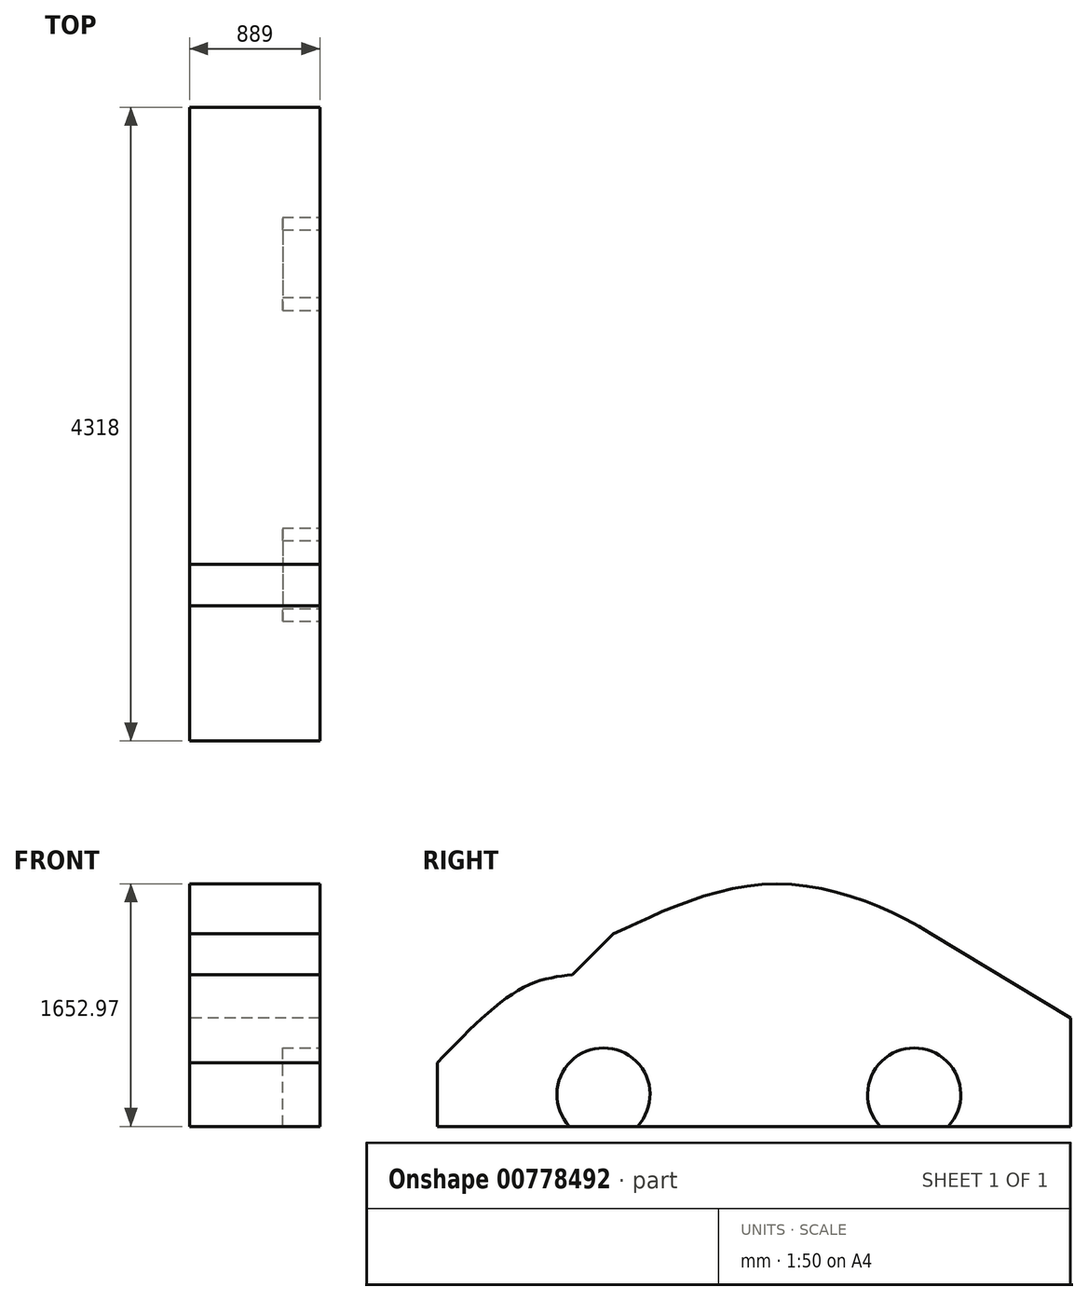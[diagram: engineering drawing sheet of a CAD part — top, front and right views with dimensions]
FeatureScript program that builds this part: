
annotation { "Feature Type Name" : "Feature", "Feature Type Description" : "" }
export const myFeature = defineFeature(function(context is Context, id is Id, definition is map)
    precondition{}
    {
        {
            var Q0;
            Q0=qCreatedBy(makeId("Right.planeOp"),FACE);
            var sketch = newSketch(context, id + "F0", { "sketchPlane" : qUnion([Q0])});
            skLineSegment(sketch, "E0.bottom", {"start": v(0, 0) * mm, "end": v(-4318, 0) * mm});
            skLineSegment(sketch, "E0.top", {"start": v(0, 1778) * mm, "end": v(-4318, 1778) * mm});
            skLineSegment(sketch, "E0.left", {"start": v(0, 0) * mm, "end": v(0, 1778) * mm});
            skLineSegment(sketch, "E0.right", {"start": v(-4318, 0) * mm, "end": v(-4318, 1778) * mm});
            skFitSpline(sketch, "E1", {"points": [v(-4318, 433.97) * mm, v(-3740.69, 941.8) * mm, v(-3396.3, 1035.18) * mm], "startDerivative": vector(1006.5, 1039.14) * mm, "endDerivative": vector(825.47, 104.2) * mm});
            skLineSegment(sketch, "E2", {"start": v(-3396.3, 1035.18) * mm, "end": v(-3116.36, 1313.4) * mm});
            skFitSpline(sketch, "E3", {"points": [v(-3116.36, 1313.4) * mm, v(-2071, 1651.44) * mm, v(-950.13, 1313.4) * mm], "startDerivative": vector(1753.15, 803.53) * mm, "endDerivative": vector(1891.45, -1155.88) * mm});
            skLineSegment(sketch, "E4", {"start": v(-950.13, 1313.4) * mm, "end": v(0, 738.14) * mm});
            skSolve(sketch);
        }
        {
            var Q0;
            {var subQ2=sQuery(id+"F0.wireOp",EDGE,"E0.bottom");Q0=makeQuery(id+"F0.imprint","IMPRINT",FACE,{"disambiguationData":[TD([[makeQuery(id+"F0.imprint","IMPRINT",EDGE,{"derivedFrom":subQ2}),-1.0]])]});}
            extrude(context, id + "F1", {"entities" : qUnion([Q0]), "depth" : 889 * mm, "offsetDistance" : 25.4 * mm});
        }
        {
            var Q0;
            Q0=makeQuery(id+"F1.opExtrude","CAP_FACE",FACE,{"disambiguationData":[OSD([sQuery(id+"F0.wireOp",EDGE,"E0.bottom"),sQuery(id+"F0.wireOp",EDGE,"E0.left"),sQuery(id+"F0.wireOp",EDGE,"E0.right"),sQuery(id+"F0.wireOp",EDGE,"E1"),sQuery(id+"F0.wireOp",EDGE,"E2"),sQuery(id+"F0.wireOp",EDGE,"E3"),sQuery(id+"F0.wireOp",EDGE,"E4")])],"isStart":false});
            var sketch = newSketch(context, id + "F2", { "sketchPlane" : qUnion([Q0])});
            skCircle(sketch, "E5", {"center": v(-3184.36, 217.56) * mm, "radius": 317.5 * mm});
            skCircle(sketch, "E6", {"center": v(-1065.77, 217.56) * mm, "radius": 317.5 * mm});
            skSolve(sketch);
        }
        {
            var Q0;
            {var subQ0=sQuery(id+"F2.wireOp",EDGE,"E6");var subQ1=makeQuery(id+"F1.opExtrude","CAP_EDGE",EDGE,{"disambiguationData":[OSD([sQuery(id+"F0.wireOp",EDGE,"E0.bottom")])],"isStart":false});var subQ2=makeQuery(id+"F2.imprint","INTERSECT",VERTEX,{"disambiguationData":[OD(0.0)],"derivedFrom":[subQ1,subQ0]});Q0=makeQuery(id+"F2.imprint","IMPRINT",FACE,{"disambiguationData":[TD([[makeQuery(id+"F2.imprint","IMPRINT",EDGE,{"disambiguationData":[TD([[subQ2,-1.0]])],"derivedFrom":subQ0}),1.0]])]});}
            var Q1;
            {var subQ0=sQuery(id+"F2.wireOp",EDGE,"E5");var subQ1=makeQuery(id+"F1.opExtrude","CAP_EDGE",EDGE,{"disambiguationData":[OSD([sQuery(id+"F0.wireOp",EDGE,"E0.bottom")])],"isStart":false});var subQ2=makeQuery(id+"F2.imprint","INTERSECT",VERTEX,{"disambiguationData":[OD(0.0)],"derivedFrom":[subQ1,subQ0]});Q1=makeQuery(id+"F2.imprint","IMPRINT",FACE,{"disambiguationData":[TD([[makeQuery(id+"F2.imprint","IMPRINT",EDGE,{"disambiguationData":[TD([[subQ2,1.0]])],"derivedFrom":subQ0}),1.0]])]});}
            extrude(context, id + "F3", {"entities" : qUnion([Q0, Q1]), "operationType" : NewBodyOperationType.REMOVE, "oppositeDirection" : true, "depth" : 254 * mm, "offsetDistance" : 25.4 * mm});
        }
    });
